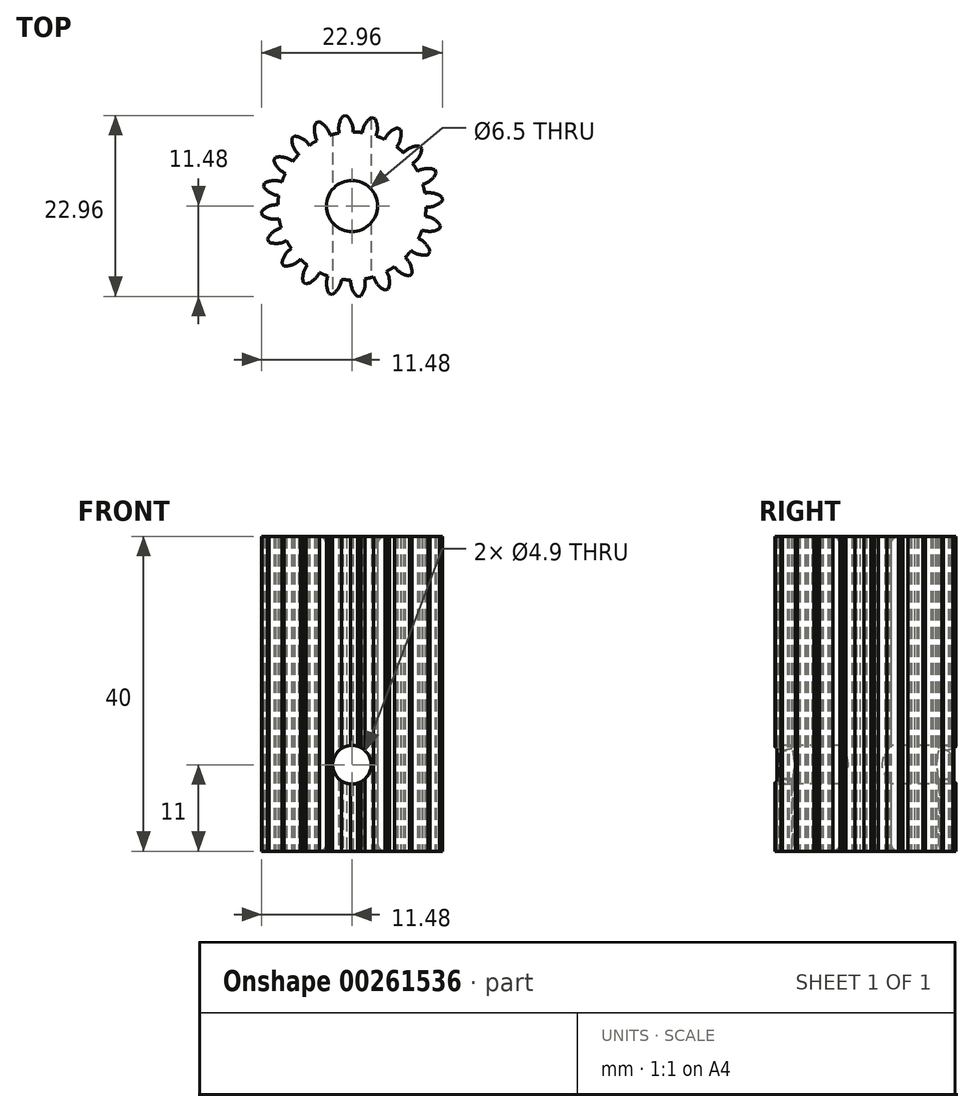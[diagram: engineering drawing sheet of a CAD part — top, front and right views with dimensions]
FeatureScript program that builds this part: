
annotation { "Feature Type Name" : "Feature", "Feature Type Description" : "" }
export const myFeature = defineFeature(function(context is Context, id is Id, definition is map)
    precondition{}
    {
        {
            assignVariable(context, id + "F0", {"name" : "GearDepth", "anyValue" : 40});
        }
        {
            var Q0;
            Q0=qCreatedBy(makeId("Top.planeOp"),FACE);
            var sketch = newSketch(context, id + "F1", { "sketchPlane" : qUnion([Q0])});
            skCircle(sketch, "E0", {"center": v(0, 0) * mm, "radius": 9.4 * mm});
            skCircle(sketch, "E1", {"center": v(0, 0) * mm, "radius": 10.45 * mm, "construction": true});
            skCircle(sketch, "E2", {"center": v(0, 0) * mm, "radius": 11.5 * mm, "construction": true});
            skLineSegment(sketch, "E3", {"start": v(0, 0) * mm, "end": v(0, 17.6) * mm, "construction": true});
            skLineSegment(sketch, "E4", {"start": v(0, 0) * mm, "end": v(-1.42, 18) * mm, "construction": true});
            skLineSegment(sketch, "E5", {"start": v(0, 10.45) * mm, "end": v(-10.54, 10.45) * mm, "construction": true});
            skLineSegment(sketch, "E6", {"start": v(0, 10.45) * mm, "end": v(-10.3, 6.7) * mm, "construction": true});
            skCircle(sketch, "E7", {"center": v(0, 10.45) * mm, "radius": 2.61 * mm, "construction": true});
            skCircle(sketch, "E8", {"center": v(-2.46, 9.56) * mm, "radius": 2.61 * mm, "construction": true});
            skArc(sketch, "E9", {"start": v(-4.91, 10.45) * mm, "mid": v(-4.92, 10.42) * mm, "end": v(-4.94, 10.39) * mm});
            skArc(sketch, "E10.trimOffspring", {"start": v(0.15, 9.4) * mm, "mid": v(-0.03, 10.54) * mm, "end": v(-0.68, 11.48) * mm});
            skArc(sketch, "E11.MirrorCS", {"start": v(-1.62, 9.27) * mm, "mid": v(-1.62, 10.41) * mm, "end": v(-1.12, 11.45) * mm});
            skLineSegment(sketch, "E12", {"start": v(-1.12, 11.45) * mm, "end": v(-0.68, 11.48) * mm});
            skArc(sketch, "E13.1.0", {"start": v(-2.76, 9) * mm, "mid": v(-3.29, 10.01) * mm, "end": v(-4.2, 10.7) * mm});
            skLineSegment(sketch, "E13.1.1", {"start": v(-4.6, 10.54) * mm, "end": v(-4.2, 10.7) * mm});
            skArc(sketch, "E13.1.2", {"start": v(-4.4, 8.31) * mm, "mid": v(-4.76, 9.4) * mm, "end": v(-4.6, 10.54) * mm});
            skArc(sketch, "E13.2.0", {"start": v(-5.4, 7.7) * mm, "mid": v(-6.22, 8.5) * mm, "end": v(-7.3, 8.89) * mm});
            skLineSegment(sketch, "E13.2.1", {"start": v(-7.64, 8.6) * mm, "end": v(-7.3, 8.89) * mm});
            skArc(sketch, "E13.2.2", {"start": v(-6.76, 6.54) * mm, "mid": v(-7.43, 7.47) * mm, "end": v(-7.64, 8.6) * mm});
            skArc(sketch, "E13.3.0", {"start": v(-7.52, 5.65) * mm, "mid": v(-8.54, 6.17) * mm, "end": v(-9.69, 6.2) * mm});
            skLineSegment(sketch, "E13.3.1", {"start": v(-9.92, 5.82) * mm, "end": v(-9.69, 6.2) * mm});
            skArc(sketch, "E13.3.2", {"start": v(-8.45, 4.13) * mm, "mid": v(-9.37, 4.81) * mm, "end": v(-9.92, 5.82) * mm});
            skArc(sketch, "E13.4.0", {"start": v(-8.9, 3.05) * mm, "mid": v(-10.03, 3.23) * mm, "end": v(-11.13, 2.9) * mm});
            skLineSegment(sketch, "E13.4.1", {"start": v(-11.23, 2.47) * mm, "end": v(-11.13, 2.9) * mm});
            skArc(sketch, "E13.4.2", {"start": v(-9.32, 1.32) * mm, "mid": v(-10.4, 1.68) * mm, "end": v(-11.23, 2.47) * mm});
            skArc(sketch, "E13.5.0", {"start": v(-9.4, 0.15) * mm, "mid": v(-10.54, -0.03) * mm, "end": v(-11.48, -0.68) * mm});
            skLineSegment(sketch, "E13.5.1", {"start": v(-11.45, -1.12) * mm, "end": v(-11.48, -0.68) * mm});
            skArc(sketch, "E13.5.2", {"start": v(-9.27, -1.62) * mm, "mid": v(-10.41, -1.62) * mm, "end": v(-11.45, -1.12) * mm});
            skArc(sketch, "E13.6.0", {"start": v(-9, -2.76) * mm, "mid": v(-10.01, -3.29) * mm, "end": v(-10.7, -4.2) * mm});
            skLineSegment(sketch, "E13.6.1", {"start": v(-10.54, -4.6) * mm, "end": v(-10.7, -4.2) * mm});
            skArc(sketch, "E13.6.2", {"start": v(-8.31, -4.4) * mm, "mid": v(-9.4, -4.76) * mm, "end": v(-10.54, -4.6) * mm});
            skArc(sketch, "E13.7.0", {"start": v(-7.7, -5.4) * mm, "mid": v(-8.5, -6.22) * mm, "end": v(-8.89, -7.3) * mm});
            skLineSegment(sketch, "E13.7.1", {"start": v(-8.6, -7.64) * mm, "end": v(-8.89, -7.3) * mm});
            skArc(sketch, "E13.7.2", {"start": v(-6.54, -6.76) * mm, "mid": v(-7.47, -7.43) * mm, "end": v(-8.6, -7.64) * mm});
            skArc(sketch, "E13.8.0", {"start": v(-5.65, -7.52) * mm, "mid": v(-6.17, -8.54) * mm, "end": v(-6.2, -9.69) * mm});
            skLineSegment(sketch, "E13.8.1", {"start": v(-5.82, -9.92) * mm, "end": v(-6.2, -9.69) * mm});
            skArc(sketch, "E13.8.2", {"start": v(-4.13, -8.45) * mm, "mid": v(-4.81, -9.37) * mm, "end": v(-5.82, -9.92) * mm});
            skArc(sketch, "E13.9.0", {"start": v(-3.05, -8.9) * mm, "mid": v(-3.23, -10.03) * mm, "end": v(-2.9, -11.13) * mm});
            skLineSegment(sketch, "E13.9.1", {"start": v(-2.47, -11.23) * mm, "end": v(-2.9, -11.13) * mm});
            skArc(sketch, "E13.9.2", {"start": v(-1.32, -9.32) * mm, "mid": v(-1.68, -10.4) * mm, "end": v(-2.47, -11.23) * mm});
            skArc(sketch, "E13.10.0", {"start": v(-0.15, -9.4) * mm, "mid": v(0.03, -10.54) * mm, "end": v(0.68, -11.48) * mm});
            skLineSegment(sketch, "E13.10.1", {"start": v(1.12, -11.45) * mm, "end": v(0.68, -11.48) * mm});
            skArc(sketch, "E13.10.2", {"start": v(1.62, -9.27) * mm, "mid": v(1.62, -10.41) * mm, "end": v(1.12, -11.45) * mm});
            skArc(sketch, "E13.11.0", {"start": v(2.76, -9) * mm, "mid": v(3.29, -10.01) * mm, "end": v(4.2, -10.7) * mm});
            skLineSegment(sketch, "E13.11.1", {"start": v(4.6, -10.54) * mm, "end": v(4.2, -10.7) * mm});
            skArc(sketch, "E13.11.2", {"start": v(4.4, -8.31) * mm, "mid": v(4.76, -9.4) * mm, "end": v(4.6, -10.54) * mm});
            skArc(sketch, "E13.12.0", {"start": v(5.4, -7.7) * mm, "mid": v(6.22, -8.5) * mm, "end": v(7.3, -8.89) * mm});
            skLineSegment(sketch, "E13.12.1", {"start": v(7.64, -8.6) * mm, "end": v(7.3, -8.89) * mm});
            skArc(sketch, "E13.12.2", {"start": v(6.76, -6.54) * mm, "mid": v(7.43, -7.47) * mm, "end": v(7.64, -8.6) * mm});
            skArc(sketch, "E13.13.0", {"start": v(7.52, -5.65) * mm, "mid": v(8.54, -6.17) * mm, "end": v(9.69, -6.2) * mm});
            skLineSegment(sketch, "E13.13.1", {"start": v(9.92, -5.82) * mm, "end": v(9.69, -6.2) * mm});
            skArc(sketch, "E13.13.2", {"start": v(8.45, -4.13) * mm, "mid": v(9.37, -4.81) * mm, "end": v(9.92, -5.82) * mm});
            skArc(sketch, "E13.14.0", {"start": v(8.9, -3.05) * mm, "mid": v(10.03, -3.23) * mm, "end": v(11.13, -2.9) * mm});
            skLineSegment(sketch, "E13.14.1", {"start": v(11.23, -2.47) * mm, "end": v(11.13, -2.9) * mm});
            skArc(sketch, "E13.14.2", {"start": v(9.32, -1.32) * mm, "mid": v(10.4, -1.68) * mm, "end": v(11.23, -2.47) * mm});
            skArc(sketch, "E13.15.0", {"start": v(9.4, -0.15) * mm, "mid": v(10.54, 0.03) * mm, "end": v(11.48, 0.68) * mm});
            skLineSegment(sketch, "E13.15.1", {"start": v(11.45, 1.12) * mm, "end": v(11.48, 0.68) * mm});
            skArc(sketch, "E13.15.2", {"start": v(9.27, 1.62) * mm, "mid": v(10.41, 1.62) * mm, "end": v(11.45, 1.12) * mm});
            skArc(sketch, "E13.16.0", {"start": v(9, 2.76) * mm, "mid": v(10.01, 3.29) * mm, "end": v(10.7, 4.2) * mm});
            skLineSegment(sketch, "E13.16.1", {"start": v(10.54, 4.6) * mm, "end": v(10.7, 4.2) * mm});
            skArc(sketch, "E13.16.2", {"start": v(8.31, 4.4) * mm, "mid": v(9.4, 4.76) * mm, "end": v(10.54, 4.6) * mm});
            skArc(sketch, "E13.17.0", {"start": v(7.7, 5.4) * mm, "mid": v(8.5, 6.22) * mm, "end": v(8.89, 7.3) * mm});
            skLineSegment(sketch, "E13.17.1", {"start": v(8.6, 7.64) * mm, "end": v(8.89, 7.3) * mm});
            skArc(sketch, "E13.17.2", {"start": v(6.54, 6.76) * mm, "mid": v(7.47, 7.43) * mm, "end": v(8.6, 7.64) * mm});
            skArc(sketch, "E13.18.0", {"start": v(5.65, 7.52) * mm, "mid": v(6.17, 8.54) * mm, "end": v(6.2, 9.69) * mm});
            skLineSegment(sketch, "E13.18.1", {"start": v(5.82, 9.92) * mm, "end": v(6.2, 9.69) * mm});
            skArc(sketch, "E13.18.2", {"start": v(4.13, 8.45) * mm, "mid": v(4.81, 9.37) * mm, "end": v(5.82, 9.92) * mm});
            skArc(sketch, "E13.19.0", {"start": v(3.05, 8.9) * mm, "mid": v(3.23, 10.03) * mm, "end": v(2.9, 11.13) * mm});
            skLineSegment(sketch, "E13.19.1", {"start": v(2.47, 11.23) * mm, "end": v(2.9, 11.13) * mm});
            skArc(sketch, "E13.19.2", {"start": v(1.32, 9.32) * mm, "mid": v(1.68, 10.4) * mm, "end": v(2.47, 11.23) * mm});
            skCircle(sketch, "E14", {"center": v(0, 0) * mm, "radius": 3.25 * mm});
            skSolve(sketch);
        }
        {
            var Q0;
            {var subQ0=sQuery(id+"F1.wireOp",EDGE,"E10.trimOffspring");Q0=makeQuery(id+"F1.imprint","IMPRINT",FACE,{"disambiguationData":[TD([[makeQuery(id+"F1.imprint","IMPRINT",EDGE,{"derivedFrom":subQ0}),1.0]])]});}
            var Q1;
            {var subQ0=sQuery(id+"F1.wireOp",EDGE,"E0");var subQ1=makeQuery(id+"F1.imprint","INTERSECT",VERTEX,{"derivedFrom":[subQ0,sQuery(id+"F1.wireOp",EDGE,"E10.trimOffspring")]});Q1=makeQuery(id+"F1.imprint","IMPRINT",FACE,{"disambiguationData":[TD([[makeQuery(id+"F1.imprint","IMPRINT",EDGE,{"disambiguationData":[TD([[subQ1,-1.0]])],"derivedFrom":subQ0}),1.0]])]});}
            var Q2;
            {var subQ0=sQuery(id+"F1.wireOp",EDGE,"E13.1.0");Q2=makeQuery(id+"F1.imprint","IMPRINT",FACE,{"disambiguationData":[TD([[makeQuery(id+"F1.imprint","IMPRINT",EDGE,{"derivedFrom":subQ0}),1.0]])]});}
            var Q3;
            {var subQ0=sQuery(id+"F1.wireOp",EDGE,"E13.2.0");Q3=makeQuery(id+"F1.imprint","IMPRINT",FACE,{"disambiguationData":[TD([[makeQuery(id+"F1.imprint","IMPRINT",EDGE,{"derivedFrom":subQ0}),1.0]])]});}
            var Q4;
            {var subQ0=sQuery(id+"F1.wireOp",EDGE,"E13.3.0");Q4=makeQuery(id+"F1.imprint","IMPRINT",FACE,{"disambiguationData":[TD([[makeQuery(id+"F1.imprint","IMPRINT",EDGE,{"derivedFrom":subQ0}),1.0]])]});}
            var Q5;
            {var subQ0=sQuery(id+"F1.wireOp",EDGE,"E13.4.0");Q5=makeQuery(id+"F1.imprint","IMPRINT",FACE,{"disambiguationData":[TD([[makeQuery(id+"F1.imprint","IMPRINT",EDGE,{"derivedFrom":subQ0}),1.0]])]});}
            var Q6;
            {var subQ0=sQuery(id+"F1.wireOp",EDGE,"E13.5.0");Q6=makeQuery(id+"F1.imprint","IMPRINT",FACE,{"disambiguationData":[TD([[makeQuery(id+"F1.imprint","IMPRINT",EDGE,{"derivedFrom":subQ0}),1.0]])]});}
            var Q7;
            {var subQ0=sQuery(id+"F1.wireOp",EDGE,"E13.6.0");Q7=makeQuery(id+"F1.imprint","IMPRINT",FACE,{"disambiguationData":[TD([[makeQuery(id+"F1.imprint","IMPRINT",EDGE,{"derivedFrom":subQ0}),1.0]])]});}
            var Q8;
            {var subQ0=sQuery(id+"F1.wireOp",EDGE,"E13.7.0");Q8=makeQuery(id+"F1.imprint","IMPRINT",FACE,{"disambiguationData":[TD([[makeQuery(id+"F1.imprint","IMPRINT",EDGE,{"derivedFrom":subQ0}),1.0]])]});}
            var Q9;
            {var subQ0=sQuery(id+"F1.wireOp",EDGE,"E13.8.0");Q9=makeQuery(id+"F1.imprint","IMPRINT",FACE,{"disambiguationData":[TD([[makeQuery(id+"F1.imprint","IMPRINT",EDGE,{"derivedFrom":subQ0}),1.0]])]});}
            var Q10;
            {var subQ0=sQuery(id+"F1.wireOp",EDGE,"E13.9.0");Q10=makeQuery(id+"F1.imprint","IMPRINT",FACE,{"disambiguationData":[TD([[makeQuery(id+"F1.imprint","IMPRINT",EDGE,{"derivedFrom":subQ0}),1.0]])]});}
            var Q11;
            {var subQ0=sQuery(id+"F1.wireOp",EDGE,"E13.10.0");Q11=makeQuery(id+"F1.imprint","IMPRINT",FACE,{"disambiguationData":[TD([[makeQuery(id+"F1.imprint","IMPRINT",EDGE,{"derivedFrom":subQ0}),1.0]])]});}
            var Q12;
            {var subQ0=sQuery(id+"F1.wireOp",EDGE,"E13.11.0");Q12=makeQuery(id+"F1.imprint","IMPRINT",FACE,{"disambiguationData":[TD([[makeQuery(id+"F1.imprint","IMPRINT",EDGE,{"derivedFrom":subQ0}),1.0]])]});}
            var Q13;
            {var subQ0=sQuery(id+"F1.wireOp",EDGE,"E13.12.0");Q13=makeQuery(id+"F1.imprint","IMPRINT",FACE,{"disambiguationData":[TD([[makeQuery(id+"F1.imprint","IMPRINT",EDGE,{"derivedFrom":subQ0}),1.0]])]});}
            var Q14;
            {var subQ0=sQuery(id+"F1.wireOp",EDGE,"E13.13.0");Q14=makeQuery(id+"F1.imprint","IMPRINT",FACE,{"disambiguationData":[TD([[makeQuery(id+"F1.imprint","IMPRINT",EDGE,{"derivedFrom":subQ0}),1.0]])]});}
            var Q15;
            {var subQ0=sQuery(id+"F1.wireOp",EDGE,"E13.14.0");Q15=makeQuery(id+"F1.imprint","IMPRINT",FACE,{"disambiguationData":[TD([[makeQuery(id+"F1.imprint","IMPRINT",EDGE,{"derivedFrom":subQ0}),1.0]])]});}
            var Q16;
            {var subQ0=sQuery(id+"F1.wireOp",EDGE,"E13.15.0");Q16=makeQuery(id+"F1.imprint","IMPRINT",FACE,{"disambiguationData":[TD([[makeQuery(id+"F1.imprint","IMPRINT",EDGE,{"derivedFrom":subQ0}),1.0]])]});}
            var Q17;
            {var subQ0=sQuery(id+"F1.wireOp",EDGE,"E13.16.0");Q17=makeQuery(id+"F1.imprint","IMPRINT",FACE,{"disambiguationData":[TD([[makeQuery(id+"F1.imprint","IMPRINT",EDGE,{"derivedFrom":subQ0}),1.0]])]});}
            var Q18;
            {var subQ0=sQuery(id+"F1.wireOp",EDGE,"E13.17.0");Q18=makeQuery(id+"F1.imprint","IMPRINT",FACE,{"disambiguationData":[TD([[makeQuery(id+"F1.imprint","IMPRINT",EDGE,{"derivedFrom":subQ0}),1.0]])]});}
            var Q19;
            {var subQ0=sQuery(id+"F1.wireOp",EDGE,"E13.18.0");Q19=makeQuery(id+"F1.imprint","IMPRINT",FACE,{"disambiguationData":[TD([[makeQuery(id+"F1.imprint","IMPRINT",EDGE,{"derivedFrom":subQ0}),1.0]])]});}
            var Q20;
            {var subQ0=sQuery(id+"F1.wireOp",EDGE,"E13.19.0");Q20=makeQuery(id+"F1.imprint","IMPRINT",FACE,{"disambiguationData":[TD([[makeQuery(id+"F1.imprint","IMPRINT",EDGE,{"derivedFrom":subQ0}),1.0]])]});}
            var Q21;
            Q21=sQuery(id+"F1.wireOp",EDGE,"E0");
            var Q22;
            Q22=sQuery(id+"F1.wireOp",EDGE,"E10.trimOffspring");
            var Q23;
            Q23=sQuery(id+"F1.wireOp",EDGE,"E12");
            var Q24;
            Q24=sQuery(id+"F1.wireOp",EDGE,"E11.MirrorCS");
            extrude(context, id + "F2", {"entities" : qUnion([Q0, Q1, Q2, Q3, Q4, Q5, Q6, Q7, Q8, Q9, Q10, Q11, Q12, Q13, Q14, Q15, Q16, Q17, Q18, Q19, Q20]), "surfaceEntities" : qUnion([Q21, Q22, Q23, Q24]), "depth" : (getVariable(context, 'GearDepth')) * mm});
        }
        {
            var Q0;
            Q0=qCreatedBy(makeId("Front.planeOp"),FACE);
            cPlane(context, id + "F3", {"entities" : qUnion([Q0]), "cplaneType" : CPlaneType.OFFSET, "offset" : 15 * mm, "width" : 150 * mm, "height" : 150 * mm});
        }
        {
            var Q0;
            Q0=qCreatedBy(id+"F3.planeOp",FACE);
            var sketch = newSketch(context, id + "F4", { "sketchPlane" : qUnion([Q0])});
            skCircle(sketch, "E15", {"center": v(0, 11) * mm, "radius": 2.45 * mm});
            skSolve(sketch);
        }
        {
            var Q0;
            Q0=makeQuery(id+"F4.imprint","IMPRINT",FACE,{"disambiguationData":[TD([[makeQuery(id+"F4.imprint","IMPRINT",EDGE,{"derivedFrom":sQuery(id+"F4.wireOp",EDGE,"E15")}),1.0]])]});
            extrude(context, id + "F5", {"entities" : qUnion([Q0]), "operationType" : NewBodyOperationType.REMOVE, "oppositeDirection" : true, "depth" : 30 * mm});
        }
        {
            var Q0;
            Q0=makeQuery(id+"F2.opExtrude","CAP_EDGE",EDGE,{"disambiguationData":[OSD([sQuery(id+"F1.wireOp",EDGE,"E14")])],"isStart":false});
            var Q1;
            Q1=makeQuery(id+"F2.opExtrude","CAP_EDGE",EDGE,{"disambiguationData":[OSD([sQuery(id+"F1.wireOp",EDGE,"E14")])],"isStart":true});
            fillet(context, id + "F6", {"entities" : qUnion([Q0, Q1]), "radius" : 1 * mm, "tangentPropagation" : true, "allowEdgeOverflow" : false});
        }
    });
